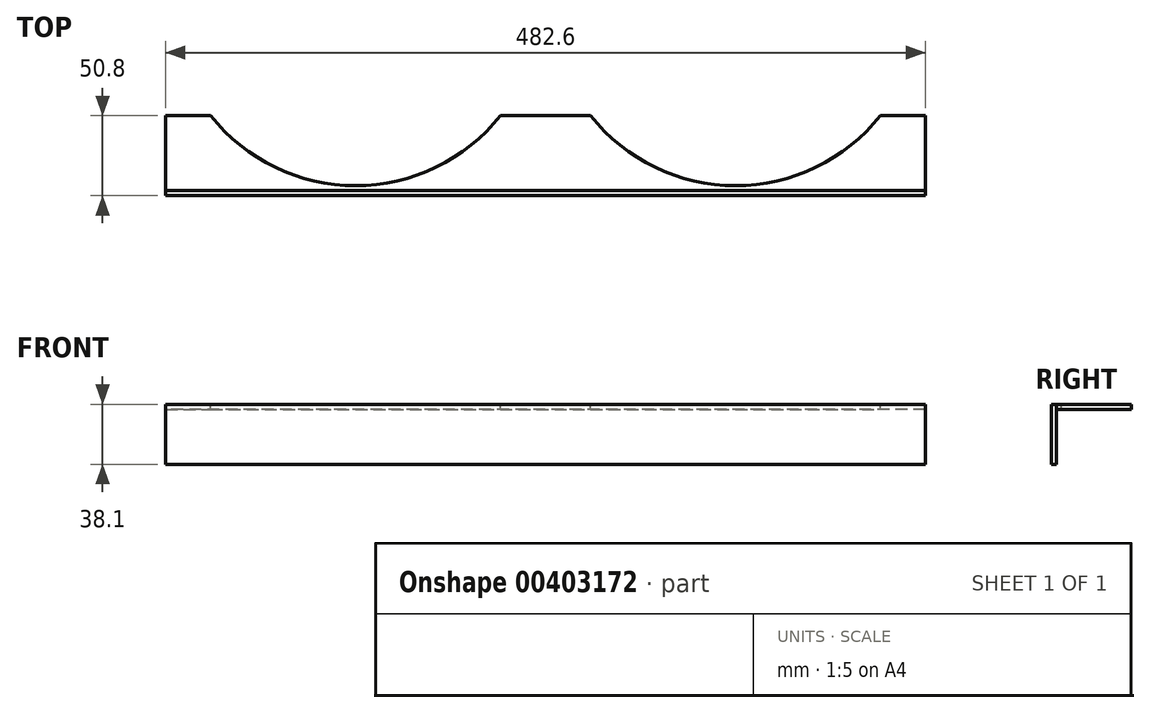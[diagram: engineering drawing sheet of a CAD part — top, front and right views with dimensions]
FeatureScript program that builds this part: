
annotation { "Feature Type Name" : "Feature", "Feature Type Description" : "" }
export const myFeature = defineFeature(function(context is Context, id is Id, definition is map)
    precondition{}
    {
        {
            var Q0;
            Q0=qCreatedBy(makeId("Top.planeOp"),FACE);
            var sketch = newSketch(context, id + "F0", { "sketchPlane" : qUnion([Q0])});
            skLineSegment(sketch, "E0.top", {"start": v(241.3, -23.81) * mm, "end": v(-241.3, -23.81) * mm});
            skLineSegment(sketch, "E0.left", {"start": v(241.3, 23.81) * mm, "end": v(241.3, -23.81) * mm});
            skLineSegment(sketch, "E0.right", {"start": v(-241.3, 23.81) * mm, "end": v(-241.3, -23.81) * mm});
            skPoint(sketch, "E0.middle", {"position": v(0, 0) * mm});
            skLineSegment(sketch, "E1.0", {"start": v(241.3, -26.99) * mm, "end": v(-241.3, -26.99) * mm});
            skLineSegment(sketch, "E2", {"start": v(-241.3, -26.99) * mm, "end": v(-241.3, -23.81) * mm});
            skLineSegment(sketch, "E3", {"start": v(241.3, -26.99) * mm, "end": v(241.3, -23.81) * mm});
            skPoint(sketch, "E4", {"position": v(120.65, -26.99) * mm});
            skPoint(sketch, "E5", {"position": v(-212.67, 23.81) * mm});
            skPoint(sketch, "E6", {"position": v(-28.63, 23.81) * mm});
            skPoint(sketch, "E7", {"position": v(-120.65, -20.64) * mm});
            skArc(sketch, "E8", {"start": v(-212.67, 23.81) * mm, "mid": v(-120.65, -20.64) * mm, "end": v(-28.63, 23.81) * mm});
            skLineSegment(sketch, "E9", {"start": v(-241.3, 23.81) * mm, "end": v(-212.67, 23.81) * mm});
            skLineSegment(sketch, "E10", {"start": v(0, 0) * mm, "end": v(0, 23.81) * mm, "construction": true});
            skArc(sketch, "E11.MirrorCS", {"start": v(212.67, 23.81) * mm, "mid": v(120.65, -20.64) * mm, "end": v(28.63, 23.81) * mm});
            skLineSegment(sketch, "E12.MirrorCS", {"start": v(241.3, 23.81) * mm, "end": v(212.67, 23.81) * mm});
            skLineSegment(sketch, "E13", {"start": v(-28.63, 23.81) * mm, "end": v(28.63, 23.81) * mm});
            skSolve(sketch);
        }
        {
            var Q0;
            Q0=makeQuery(id+"F0.imprint","IMPRINT",FACE,{"disambiguationData":[TD([[makeQuery(id+"F0.imprint","IMPRINT",EDGE,{"derivedFrom":sQuery(id+"F0.wireOp",EDGE,"E0.top")}),-1.0]])]});
            extrude(context, id + "F1", {"entities" : qUnion([Q0]), "oppositeDirection" : true, "depth" : 3.17 * mm});
        }
        {
            var Q0;
            Q0=makeQuery(id+"F0.imprint","IMPRINT",FACE,{"disambiguationData":[TD([[makeQuery(id+"F0.imprint","IMPRINT",EDGE,{"derivedFrom":sQuery(id+"F0.wireOp",EDGE,"E0.top")}),1.0]])]});
            extrude(context, id + "F2", {"entities" : qUnion([Q0]), "oppositeDirection" : true, "depth" : 38.1 * mm});
        }
    });
